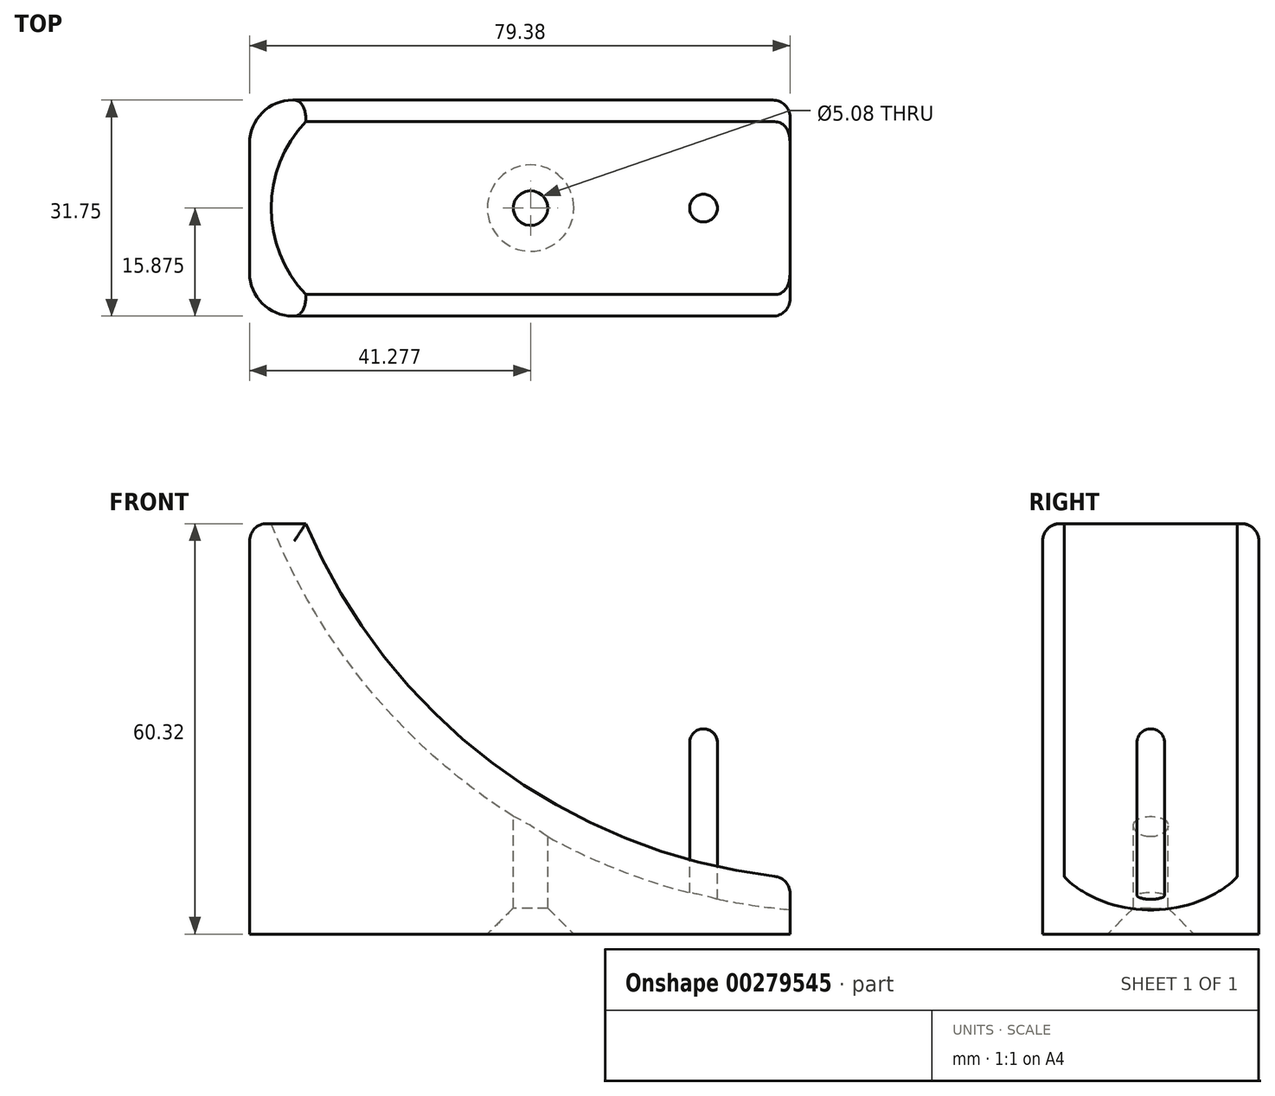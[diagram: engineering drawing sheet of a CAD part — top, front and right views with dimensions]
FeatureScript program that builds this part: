
annotation { "Feature Type Name" : "Feature", "Feature Type Description" : "" }
export const myFeature = defineFeature(function(context is Context, id is Id, definition is map)
    precondition{}
    {
        {
            var Q0;
            Q0=qCreatedBy(makeId("Front.planeOp"),FACE);
            var sketch = newSketch(context, id + "F0", { "sketchPlane" : qUnion([Q0])});
            skLineSegment(sketch, "E0.top", {"start": v(39.69, -30.16) * mm, "end": v(-39.69, -30.16) * mm});
            skLineSegment(sketch, "E0.right", {"start": v(-39.69, 30.16) * mm, "end": v(-39.69, -30.16) * mm});
            skPoint(sketch, "E0.middle", {"position": v(0, 0) * mm});
            skPoint(sketch, "E1.first.point", {"position": v(-32.66, 93.42) * mm});
            skPoint(sketch, "E1.second.point", {"position": v(62.25, 146.17) * mm});
            skPoint(sketch, "E1.third.point", {"position": v(106.42, 0) * mm});
            skPoint(sketch, "E2.first.point", {"position": v(-31.43, 30.16) * mm});
            skPoint(sketch, "E2.second.point", {"position": v(39.69, -21.9) * mm});
            skPoint(sketch, "E2.third.point", {"position": v(117.57, 112.93) * mm});
            skArc(sketch, "E3", {"start": v(-31.43, 30.16) * mm, "mid": v(-3.08, -5.71) * mm, "end": v(39.69, -21.9) * mm});
            skLineSegment(sketch, "E4", {"start": v(-31.43, 30.16) * mm, "end": v(-39.69, 30.16) * mm});
            skLineSegment(sketch, "E5", {"start": v(39.69, -21.9) * mm, "end": v(39.69, -30.16) * mm});
            skSolve(sketch);
        }
        {
            var Q0;
            Q0=makeQuery(id+"F0.imprint","IMPRINT",FACE,{"disambiguationData":[TD([[makeQuery(id+"F0.imprint","IMPRINT",EDGE,{"derivedFrom":sQuery(id+"F0.wireOp",EDGE,"E0.top")}),-1.0]])]});
            extrude(context, id + "F1", {"entities" : qUnion([Q0]), "depth" : 31.75 * mm});
        }
        {
            var Q0;
            Q0=makeQuery(id+"F1.opExtrude","SWEPT_EDGE",EDGE,{"disambiguationData":[OSD([sQuery(id+"F0.wireOp",EDGE,"E3"),sQuery(id+"F0.wireOp",EDGE,"E4")])]});
            cPoint(context, id + "F2", {"entities" : qUnion([Q0]), "parameter" : 0.5});
        }
        {
            var Q0;
            Q0=qCreatedBy(makeId("Front.planeOp"),FACE);
            var Q1;
            Q1 = qCreatedBy(id + "F2" ,VERTEX);
            cPlane(context, id + "F3", {"entities" : qUnion([Q0, Q1]), "cplaneType" : CPlaneType.PLANE_POINT, "offset" : 25.4 * mm, "width" : 152.4 * mm, "height" : 152.4 * mm});
        }
        {
            var Q0;
            Q0=qCreatedBy(id+"F3.planeOp",FACE);
            var sketch = newSketch(context, id + "F4", { "sketchPlane" : qUnion([Q0])});
            skCircle(sketch, "E6", {"center": v(47.56, 63.45) * mm, "radius": 85.73 * mm, "construction": true});
            skCircle(sketch, "E7", {"center": v(47.56, 63.45) * mm, "radius": 88.9 * mm, "construction": true});
            skCircle(sketch, "E8", {"center": v(47.56, 63.45) * mm, "radius": 79.38 * mm, "construction": true});
            skSolve(sketch);
        }
        {
            var Q0;
            Q0=makeQuery(id+"F1.opExtrude","SWEPT_FACE",FACE,{"disambiguationData":[OSD([sQuery(id+"F0.wireOp",EDGE,"E4")])]});
            var sketch = newSketch(context, id + "F5", { "sketchPlane" : qUnion([Q0])});
            skCircle(sketch, "E9", {"center": v(-18.1, -15.88) * mm, "radius": 18.41 * mm});
            skSolve(sketch);
        }
        {
            var Q0;
            Q0=qCreatedBy(id+"F3.planeOp",FACE);
            var sketch = newSketch(context, id + "F6", { "sketchPlane" : qUnion([Q0])});
            skCircle(sketch, "E10", {"center": v(47.56, 63.45) * mm, "radius": 73.62 * mm, "construction": true});
            skSolve(sketch);
        }
        {
            var Q0;
            {var subQ0=sQuery(id+"F5.wireOp",EDGE,"E9");var subQ1=makeQuery(id+"F1.opExtrude","SWEPT_EDGE",EDGE,{"disambiguationData":[OSD([sQuery(id+"F0.wireOp",EDGE,"E3"),sQuery(id+"F0.wireOp",EDGE,"E4")])]});var subQ2=makeQuery(id+"F5.imprint","INTERSECT",VERTEX,{"disambiguationData":[OD(0.0)],"derivedFrom":[subQ1,subQ0]});Q0=makeQuery(id+"F5.imprint","IMPRINT",FACE,{"disambiguationData":[TD([[makeQuery(id+"F5.imprint","IMPRINT",EDGE,{"disambiguationData":[TD([[subQ2,-1.0]])],"derivedFrom":subQ0}),1.0]])]});}
            var Q1;
            Q1=sQuery(id+"F6.wireOp",EDGE,"E10");
            revolve(context, id + "F7", {"entities" : qUnion([Q0]), "axis" : qUnion([Q1]), "revolveType" : RevolveType.FULL});
        }
        {
            var Q0;
            Q0=makeQuery(id+"F7.opRevolve","SWEPT_BODY",BODY,{"disambiguationData":[OSD([sQuery(id+"F0.wireOp",EDGE,"E3"),sQuery(id+"F0.wireOp",EDGE,"E4"),sQuery(id+"F5.wireOp",EDGE,"E9")])]});
            var Q1;
            Q1=makeQuery(id+"F1.opExtrude","SWEPT_BODY",BODY,{"disambiguationData":[OSD([sQuery(id+"F0.wireOp",EDGE,"E0.top"),sQuery(id+"F0.wireOp",EDGE,"E0.right"),sQuery(id+"F0.wireOp",EDGE,"E3"),sQuery(id+"F0.wireOp",EDGE,"E4"),sQuery(id+"F0.wireOp",EDGE,"E5")])]});
            booleanBodies(context, id + "F8", {"operationType" : BooleanOperationType.SUBTRACTION, "tools" : qUnion([Q0]), "targets" : qUnion([Q1])});
        }
        {
            var Q0;
            Q0=makeQuery(id+"F1.opExtrude","CAP_EDGE",EDGE,{"disambiguationData":[OSD([sQuery(id+"F0.wireOp",EDGE,"E0.right")])],"isStart":false});
            var Q1;
            Q1=makeQuery(id+"F1.opExtrude","CAP_EDGE",EDGE,{"disambiguationData":[OSD([sQuery(id+"F0.wireOp",EDGE,"E0.right")])],"isStart":true});
            fillet(context, id + "F9", {"entities" : qUnion([Q0, Q1]), "radius" : 6.35 * mm, "tangentPropagation" : true, "allowEdgeOverflow" : false});
        }
        {
            var Q0;
            Q0=makeQuery(id+"F1.opExtrude","CAP_EDGE",EDGE,{"disambiguationData":[OSD([sQuery(id+"F0.wireOp",EDGE,"E5")])],"isStart":false});
            var Q1;
            Q1=makeQuery(id+"F1.opExtrude","CAP_EDGE",EDGE,{"disambiguationData":[OSD([sQuery(id+"F0.wireOp",EDGE,"E5")])],"isStart":true});
            fillet(context, id + "F10", {"entities" : qUnion([Q0, Q1]), "radius" : 2.54 * mm, "tangentPropagation" : true, "allowEdgeOverflow" : false});
        }
        {
            var Q0;
            Q0=makeQuery(id+"F1.opExtrude","CAP_EDGE",EDGE,{"disambiguationData":[OSD([sQuery(id+"F0.wireOp",EDGE,"E3")])],"isStart":false});
            var Q1;
            Q1=makeQuery(id+"F1.opExtrude","CAP_EDGE",EDGE,{"disambiguationData":[OSD([sQuery(id+"F0.wireOp",EDGE,"E3")])],"isStart":true});
            var Q2;
            Q2=makeQuery(id+"F9.opFillet","BLEND_EDGE",EDGE,{"blendedFrom":[makeQuery(id+"F1.opExtrude","CAP_EDGE",EDGE,{"disambiguationData":[OSD([sQuery(id+"F0.wireOp",EDGE,"E0.right")])],"isStart":false}),makeQuery(id+"F1.opExtrude","SWEPT_FACE",FACE,{"disambiguationData":[OSD([sQuery(id+"F0.wireOp",EDGE,"E4")])]})],"blendedInto":[makeQuery(id+"F1.opExtrude","SWEPT_FACE",FACE,{"disambiguationData":[OSD([sQuery(id+"F0.wireOp",EDGE,"E4")])]})]});
            var Q3;
            Q3=makeQuery(id+"F1.opExtrude","SWEPT_EDGE",EDGE,{"disambiguationData":[OSD([sQuery(id+"F0.wireOp",EDGE,"E0.right"),sQuery(id+"F0.wireOp",EDGE,"E4")])]});
            var Q4;
            Q4=makeQuery(id+"F9.opFillet","BLEND_EDGE",EDGE,{"blendedFrom":[makeQuery(id+"F1.opExtrude","CAP_EDGE",EDGE,{"disambiguationData":[OSD([sQuery(id+"F0.wireOp",EDGE,"E0.right")])],"isStart":true}),makeQuery(id+"F1.opExtrude","SWEPT_FACE",FACE,{"disambiguationData":[OSD([sQuery(id+"F0.wireOp",EDGE,"E4")])]})],"blendedInto":[makeQuery(id+"F1.opExtrude","SWEPT_FACE",FACE,{"disambiguationData":[OSD([sQuery(id+"F0.wireOp",EDGE,"E4")])]})]});
            var Q5;
            Q5=makeQuery(id+"F1.opExtrude","CAP_EDGE",EDGE,{"disambiguationData":[OSD([sQuery(id+"F0.wireOp",EDGE,"E4")])],"isStart":true});
            var Q6;
            Q6=makeQuery(id+"F1.opExtrude","CAP_EDGE",EDGE,{"disambiguationData":[OSD([sQuery(id+"F0.wireOp",EDGE,"E4")])],"isStart":false});
            fillet(context, id + "F11", {"entities" : qUnion([Q0, Q1, Q2, Q3, Q4, Q5, Q6]), "radius" : 2.54 * mm, "tangentPropagation" : true, "allowEdgeOverflow" : false});
        }
        {
            var Q0;
            Q0=qCreatedBy(makeId("Top.planeOp"),FACE);
            var sketch = newSketch(context, id + "F12", { "sketchPlane" : qUnion([Q0])});
            skCircle(sketch, "E11", {"center": v(1.59, -15.88) * mm, "radius": 2.54 * mm});
            skCircle(sketch, "E12", {"center": v(26.99, -15.88) * mm, "radius": 2.03 * mm});
            skSolve(sketch);
        }
        {
            var Q0;
            Q0=makeQuery(id+"F12.imprint","IMPRINT",FACE,{"disambiguationData":[TD([[makeQuery(id+"F12.imprint","IMPRINT",EDGE,{"derivedFrom":sQuery(id+"F12.wireOp",EDGE,"E11")}),1.0]])]});
            extrude(context, id + "F13", {"entities" : qUnion([Q0]), "operationType" : NewBodyOperationType.REMOVE, "oppositeDirection" : true, "depth" : 30.73 * mm});
        }
        {
            var Q0;
            Q0=makeQuery(id+"F12.imprint","IMPRINT",FACE,{"disambiguationData":[TD([[makeQuery(id+"F12.imprint","IMPRINT",EDGE,{"derivedFrom":sQuery(id+"F12.wireOp",EDGE,"E12")}),1.0]])]});
            extrude(context, id + "F14", {"entities" : qUnion([Q0]), "operationType" : NewBodyOperationType.ADD, "endBound" : BoundingType.UP_TO_NEXT, "oppositeDirection" : true, "depth" : 25.4 * mm});
        }
        {
            var Q0;
            Q0=makeQuery(id+"F14.opExtrude","CAP_EDGE",EDGE,{"disambiguationData":[OSD([sQuery(id+"F12.wireOp",EDGE,"E12")])],"isStart":true});
            fillet(context, id + "F15", {"entities" : qUnion([Q0]), "radius" : 2.03 * mm, "tangentPropagation" : true, "allowEdgeOverflow" : false});
        }
        {
            var Q0;
            Q0=makeQuery(id+"F13.boolean.opBoolean","INTERSECT",EDGE,{"derivedFrom":[makeQuery(id+"F1.opExtrude","SWEPT_FACE",FACE,{"disambiguationData":[OSD([sQuery(id+"F0.wireOp",EDGE,"E0.top")])]}),makeQuery(id+"F13.opExtrude","SWEPT_FACE",FACE,{"disambiguationData":[OSD([sQuery(id+"F12.wireOp",EDGE,"E11")])]})]});
            chamfer(context, id + "F16", {"entities" : qUnion([Q0]), "width" : 3.8 * mm, "tangentPropagation" : true});
        }
    });
